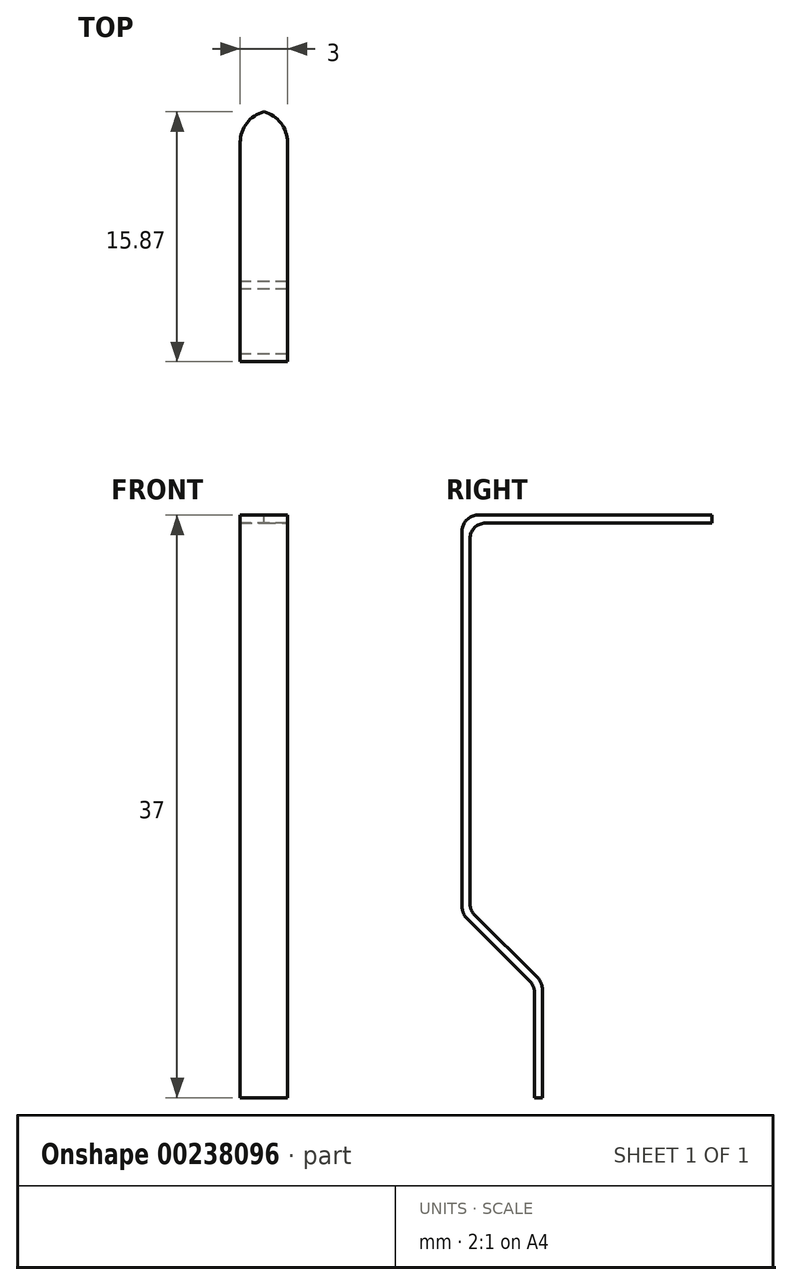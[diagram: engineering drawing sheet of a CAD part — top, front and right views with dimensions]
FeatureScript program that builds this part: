
annotation { "Feature Type Name" : "Feature", "Feature Type Description" : "" }
export const myFeature = defineFeature(function(context is Context, id is Id, definition is map)
    precondition{}
    {
        {
            var Q0;
            Q0=qCreatedBy(makeId("Right.planeOp"),FACE);
            var sketch = newSketch(context, id + "F0", { "sketchPlane" : qUnion([Q0])});
            skLineSegment(sketch, "E0", {"start": v(0, 0) * mm, "end": v(0, 6.69) * mm});
            skLineSegment(sketch, "E1", {"start": v(-0.3, 7.4) * mm, "end": v(-4.3, 11.4) * mm});
            skLineSegment(sketch, "E2", {"start": v(-4.6, 12.11) * mm, "end": v(-4.6, 36) * mm});
            skLineSegment(sketch, "E3", {"start": v(-3.6, 37) * mm, "end": v(11.34, 37) * mm});
            skLineSegment(sketch, "E4", {"start": v(11.34, 37) * mm, "end": v(11.34, 36.5) * mm});
            skLineSegment(sketch, "E5", {"start": v(11.34, 36.5) * mm, "end": v(-3.1, 36.5) * mm});
            skLineSegment(sketch, "E6", {"start": v(0, 0) * mm, "end": v(0.5, 0) * mm});
            skLineSegment(sketch, "E7", {"start": v(0.5, 0) * mm, "end": v(0.5, 6.9) * mm});
            skLineSegment(sketch, "E8", {"start": v(0.2, 7.6) * mm, "end": v(-3.8, 11.61) * mm});
            skLineSegment(sketch, "E9", {"start": v(-4.1, 35.5) * mm, "end": v(-4.1, 12.32) * mm});
            skPoint(sketch, "E10.start.orphan", {"position": v(-2.3, 9.4) * mm});
            skPoint(sketch, "E11.visualSharp", {"position": v(-4.1, 36.5) * mm});
            skArc(sketch, "E11.filletArc", {"start": v(-3.1, 36.5) * mm, "mid": v(-3.8, 36.2) * mm, "end": v(-4.1, 35.5) * mm});
            skPoint(sketch, "E12.visualSharp", {"position": v(-4.6, 37) * mm});
            skArc(sketch, "E12.filletArc", {"start": v(-3.6, 37) * mm, "mid": v(-4.3, 36.7) * mm, "end": v(-4.6, 36) * mm});
            skPoint(sketch, "E13.visualSharp", {"position": v(-4.1, 11.9) * mm});
            skArc(sketch, "E13.filletArc", {"start": v(-4.1, 12.32) * mm, "mid": v(-4.02, 11.94) * mm, "end": v(-3.8, 11.61) * mm});
            skPoint(sketch, "E14.visualSharp", {"position": v(-4.6, 11.7) * mm});
            skArc(sketch, "E14.filletArc", {"start": v(-4.6, 12.11) * mm, "mid": v(-4.52, 11.73) * mm, "end": v(-4.3, 11.4) * mm});
            skPoint(sketch, "E15.visualSharp", {"position": v(0.5, 7.3) * mm});
            skArc(sketch, "E15.filletArc", {"start": v(0.5, 6.9) * mm, "mid": v(0.42, 7.28) * mm, "end": v(0.2, 7.6) * mm});
            skPoint(sketch, "E16.visualSharp", {"position": v(0, 7.1) * mm});
            skArc(sketch, "E16.filletArc", {"start": v(0, 6.69) * mm, "mid": v(-0.08, 7.07) * mm, "end": v(-0.3, 7.4) * mm});
            skSolve(sketch);
        }
        {
            var Q0;
            Q0 = qSketchRegion(id + "F0", true);
            extrude(context, id + "F1", {"entities" : qUnion([Q0]), "endBound" : BoundingType.SYMMETRIC, "depth" : 3 * mm});
        }
        {
            var Q0;
            Q0=makeQuery(id+"F1.opExtrude","SWEPT_FACE",FACE,{"disambiguationData":[OSD([sQuery(id+"F0.wireOp",EDGE,"E3")])]});
            var sketch = newSketch(context, id + "F2", { "sketchPlane" : qUnion([Q0])});
            skLineSegment(sketch, "E17", {"start": v(-1.5, 9.1) * mm, "end": v(-1.5, 9.34) * mm});
            skPoint(sketch, "E18.visualSharp", {"position": v(-1.5, 11.34) * mm});
            skArc(sketch, "E18.filletArc", {"start": v(0, 11.27) * mm, "mid": v(-1.08, 10.56) * mm, "end": v(-1.5, 9.34) * mm});
            skPoint(sketch, "E19.visualSharp", {"position": v(1.5, 11.34) * mm});
            skArc(sketch, "E19.filletArc", {"start": v(1.5, 9.34) * mm, "mid": v(1.08, 10.56) * mm, "end": v(0, 11.27) * mm});
            skLineSegment(sketch, "E20", {"start": v(-1.5, 9.34) * mm, "end": v(-1.5, 11.34) * mm});
            skLineSegment(sketch, "E21", {"start": v(1.5, 11.34) * mm, "end": v(-1.5, 11.34) * mm});
            skLineSegment(sketch, "E22", {"start": v(1.5, 11.34) * mm, "end": v(1.5, 9.34) * mm});
            skSolve(sketch);
        }
        {
            var Q0;
            Q0 = qSketchRegion(id + "F2", true);
            extrude(context, id + "F3", {"entities" : qUnion([Q0]), "operationType" : NewBodyOperationType.REMOVE, "oppositeDirection" : true, "depth" : 25 * mm});
        }
    });
